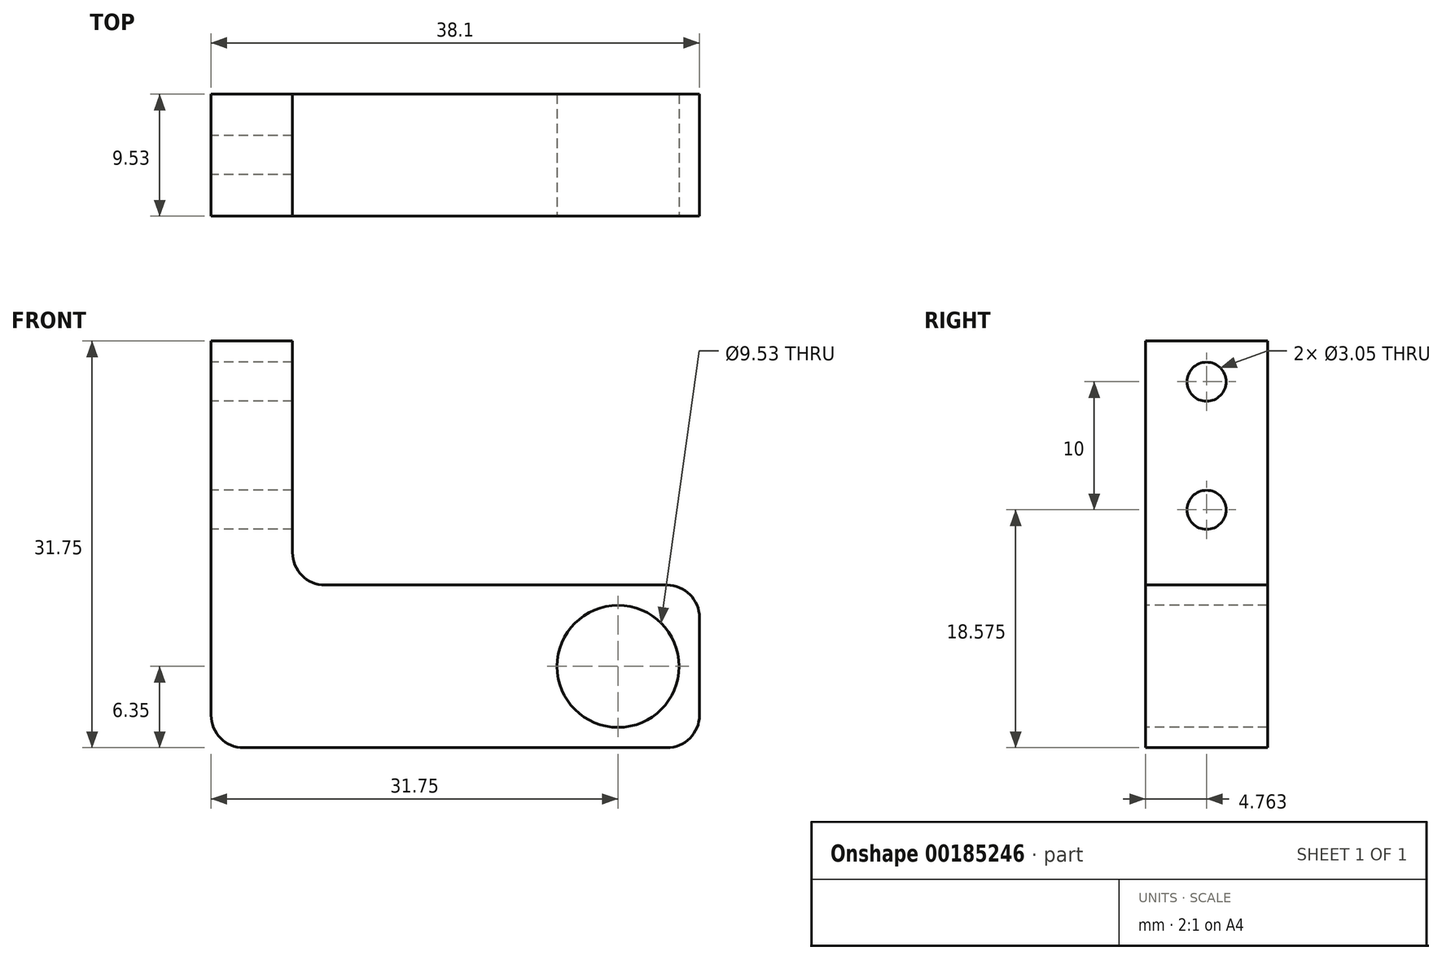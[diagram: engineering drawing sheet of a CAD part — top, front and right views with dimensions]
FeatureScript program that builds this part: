
annotation { "Feature Type Name" : "Feature", "Feature Type Description" : "" }
export const myFeature = defineFeature(function(context is Context, id is Id, definition is map)
    precondition{}
    {
        {
            var Q0;
            Q0=qCreatedBy(makeId("Front.planeOp"),FACE);
            var sketch = newSketch(context, id + "F0", { "sketchPlane" : qUnion([Q0])});
            skLineSegment(sketch, "E0", {"start": v(6.35, 31.75) * mm, "end": v(6.35, 12.7) * mm});
            skLineSegment(sketch, "E1", {"start": v(6.35, 12.7) * mm, "end": v(38.1, 12.7) * mm});
            skLineSegment(sketch, "E2", {"start": v(38.1, 12.7) * mm, "end": v(38.1, 0) * mm});
            skLineSegment(sketch, "E3", {"start": v(38.1, 0) * mm, "end": v(0, 0) * mm});
            skLineSegment(sketch, "E4", {"start": v(0, 0) * mm, "end": v(0, 31.75) * mm});
            skLineSegment(sketch, "E5", {"start": v(0, 31.75) * mm, "end": v(6.35, 31.75) * mm});
            skSolve(sketch);
        }
        {
            var Q0;
            Q0=makeQuery(id+"F0.imprint","IMPRINT",FACE,{"disambiguationData":[TD([[makeQuery(id+"F0.imprint","IMPRINT",EDGE,{"derivedFrom":sQuery(id+"F0.wireOp",EDGE,"E0")}),-1.0]])]});
            extrude(context, id + "F1", {"entities" : qUnion([Q0]), "oppositeDirection" : true, "depth" : 9.52 * mm});
        }
        {
            var Q0;
            Q0=qCreatedBy(makeId("Front.planeOp"),FACE);
            var sketch = newSketch(context, id + "F2", { "sketchPlane" : qUnion([Q0])});
            skCircle(sketch, "E6", {"center": v(31.75, 6.35) * mm, "radius": 4.76 * mm});
            skSolve(sketch);
        }
        {
            var Q0;
            Q0=makeQuery(id+"F2.imprint","IMPRINT",FACE,{"disambiguationData":[TD([[makeQuery(id+"F2.imprint","IMPRINT",EDGE,{"derivedFrom":sQuery(id+"F2.wireOp",EDGE,"E6")}),1.0]])]});
            extrude(context, id + "F3", {"entities" : qUnion([Q0]), "operationType" : NewBodyOperationType.REMOVE, "endBound" : BoundingType.THROUGH_ALL, "oppositeDirection" : true, "depth" : 25.4 * mm});
        }
        {
            var Q0;
            Q0=qCreatedBy(makeId("Right.planeOp"),FACE);
            var sketch = newSketch(context, id + "F4", { "sketchPlane" : qUnion([Q0])});
            skCircle(sketch, "E7", {"center": v(4.76, 28.57) * mm, "radius": 1.52 * mm});
            skCircle(sketch, "E8", {"center": v(4.76, 18.58) * mm, "radius": 1.52 * mm});
            skSolve(sketch);
        }
        {
            var Q0;
            Q0 = qSketchRegion(id + "F4", true);
            extrude(context, id + "F5", {"entities" : qUnion([Q0]), "operationType" : NewBodyOperationType.REMOVE, "depth" : 25.4 * mm});
        }
        {
            var Q0;
            Q0=makeQuery(id+"F1.opExtrude","SWEPT_EDGE",EDGE,{"disambiguationData":[OSD([sQuery(id+"F0.wireOp",EDGE,"E3"),sQuery(id+"F0.wireOp",EDGE,"E4")])]});
            var Q1;
            Q1=makeQuery(id+"F1.opExtrude","SWEPT_EDGE",EDGE,{"disambiguationData":[OSD([sQuery(id+"F0.wireOp",EDGE,"E2"),sQuery(id+"F0.wireOp",EDGE,"E3")])]});
            var Q2;
            Q2=makeQuery(id+"F1.opExtrude","SWEPT_EDGE",EDGE,{"disambiguationData":[OSD([sQuery(id+"F0.wireOp",EDGE,"E1"),sQuery(id+"F0.wireOp",EDGE,"E2")])]});
            var Q3;
            Q3=makeQuery(id+"F1.opExtrude","SWEPT_EDGE",EDGE,{"disambiguationData":[OSD([sQuery(id+"F0.wireOp",EDGE,"E0"),sQuery(id+"F0.wireOp",EDGE,"E1")])]});
            fillet(context, id + "F6", {"entities" : qUnion([Q0, Q1, Q2, Q3]), "radius" : 2.54 * mm, "tangentPropagation" : true, "allowEdgeOverflow" : false});
        }
    });
